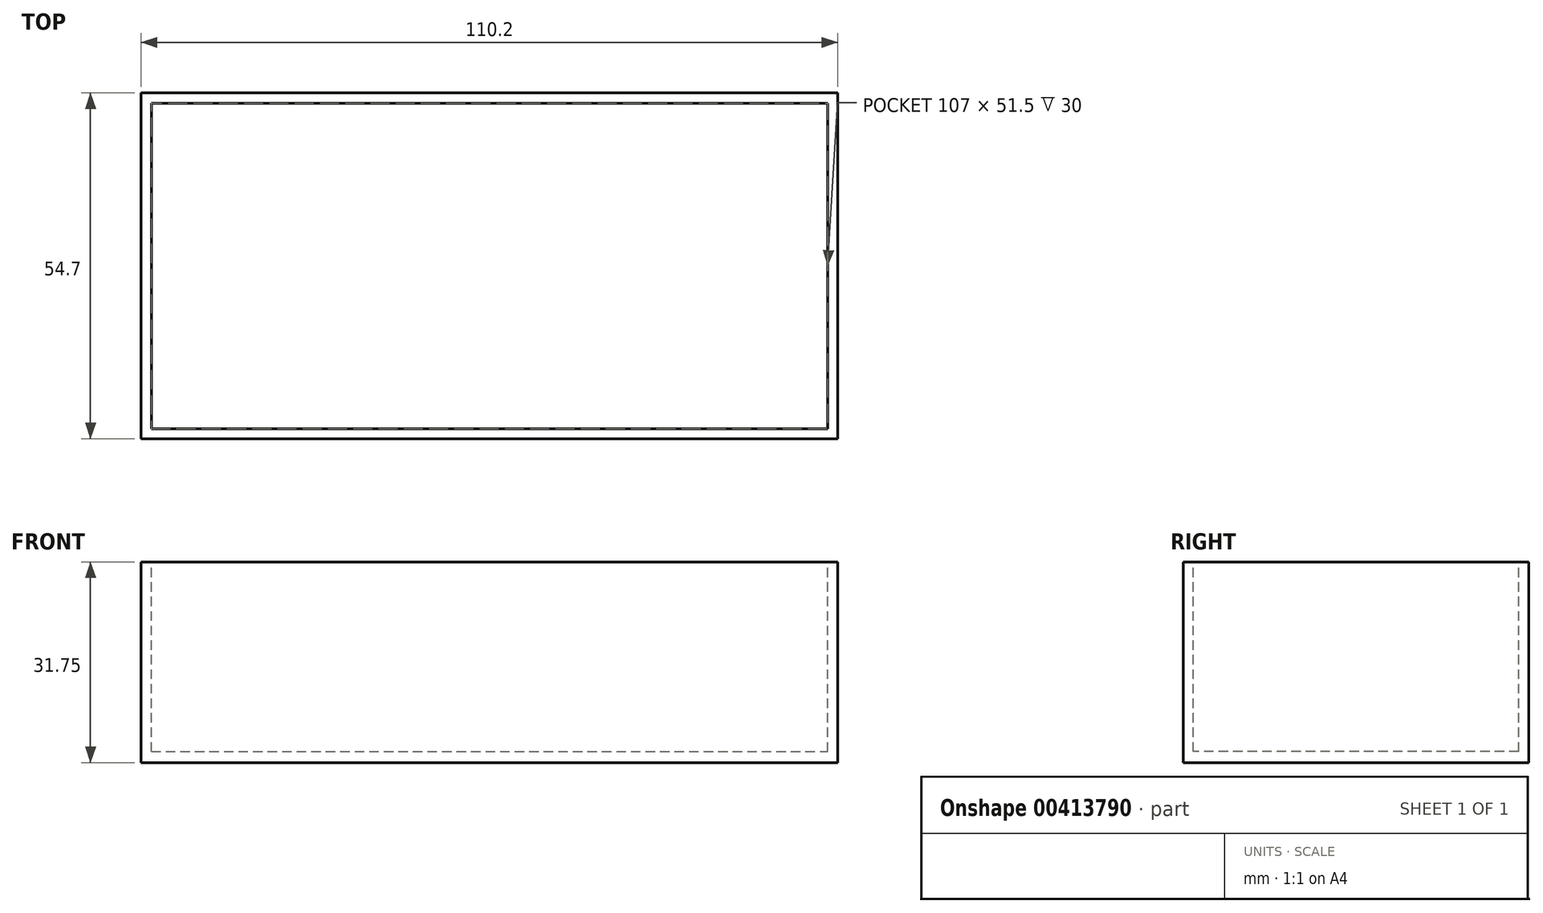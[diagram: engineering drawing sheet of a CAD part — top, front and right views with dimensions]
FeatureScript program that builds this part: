
annotation { "Feature Type Name" : "Feature", "Feature Type Description" : "" }
export const myFeature = defineFeature(function(context is Context, id is Id, definition is map)
    precondition{}
    {
        {
            var Q0;
            Q0=qCreatedBy(makeId("Top.planeOp"),FACE);
            var sketch = newSketch(context, id + "F0", { "sketchPlane" : qUnion([Q0])});
            skLineSegment(sketch, "E0.bottom", {"start": v(-54.85, 21.27) * mm, "end": v(55.35, 21.27) * mm});
            skLineSegment(sketch, "E0.top", {"start": v(-54.85, -33.43) * mm, "end": v(55.35, -33.43) * mm});
            skLineSegment(sketch, "E0.left", {"start": v(-54.85, 21.27) * mm, "end": v(-54.85, -33.43) * mm});
            skLineSegment(sketch, "E0.right", {"start": v(55.35, 21.27) * mm, "end": v(55.35, -33.43) * mm});
            skSolve(sketch);
        }
        {
            var Q0;
            Q0=makeQuery(id+"F0.imprint","IMPRINT",FACE,{"disambiguationData":[TD([[makeQuery(id+"F0.imprint","IMPRINT",EDGE,{"derivedFrom":sQuery(id+"F0.wireOp",EDGE,"E0.bottom")}),-1.0]])]});
            extrude(context, id + "F1", {"entities" : qUnion([Q0]), "depth" : 31.75 * mm});
        }
        {
            var Q0;
            Q0=makeQuery(id+"F1.opExtrude","CAP_FACE",FACE,{"disambiguationData":[OSD([sQuery(id+"F0.wireOp",EDGE,"E0.bottom"),sQuery(id+"F0.wireOp",EDGE,"E0.top"),sQuery(id+"F0.wireOp",EDGE,"E0.left"),sQuery(id+"F0.wireOp",EDGE,"E0.right")])],"isStart":false});
            var sketch = newSketch(context, id + "F2", { "sketchPlane" : qUnion([Q0])});
            skLineSegment(sketch, "E1.bottom", {"start": v(-53.25, 19.67) * mm, "end": v(53.75, 19.67) * mm});
            skLineSegment(sketch, "E1.top", {"start": v(-53.25, -31.83) * mm, "end": v(53.75, -31.83) * mm});
            skLineSegment(sketch, "E1.left", {"start": v(-53.25, 19.67) * mm, "end": v(-53.25, -31.83) * mm});
            skLineSegment(sketch, "E1.right", {"start": v(53.75, 19.67) * mm, "end": v(53.75, -31.83) * mm});
            skSolve(sketch);
        }
        {
            var Q0;
            Q0=makeQuery(id+"F2.imprint","IMPRINT",FACE,{"disambiguationData":[TD([[makeQuery(id+"F2.imprint","IMPRINT",EDGE,{"derivedFrom":sQuery(id+"F2.wireOp",EDGE,"E1.bottom")}),-1.0]])]});
            extrude(context, id + "F3", {"entities" : qUnion([Q0]), "operationType" : NewBodyOperationType.REMOVE, "depth" : -30 * mm});
        }
    });
